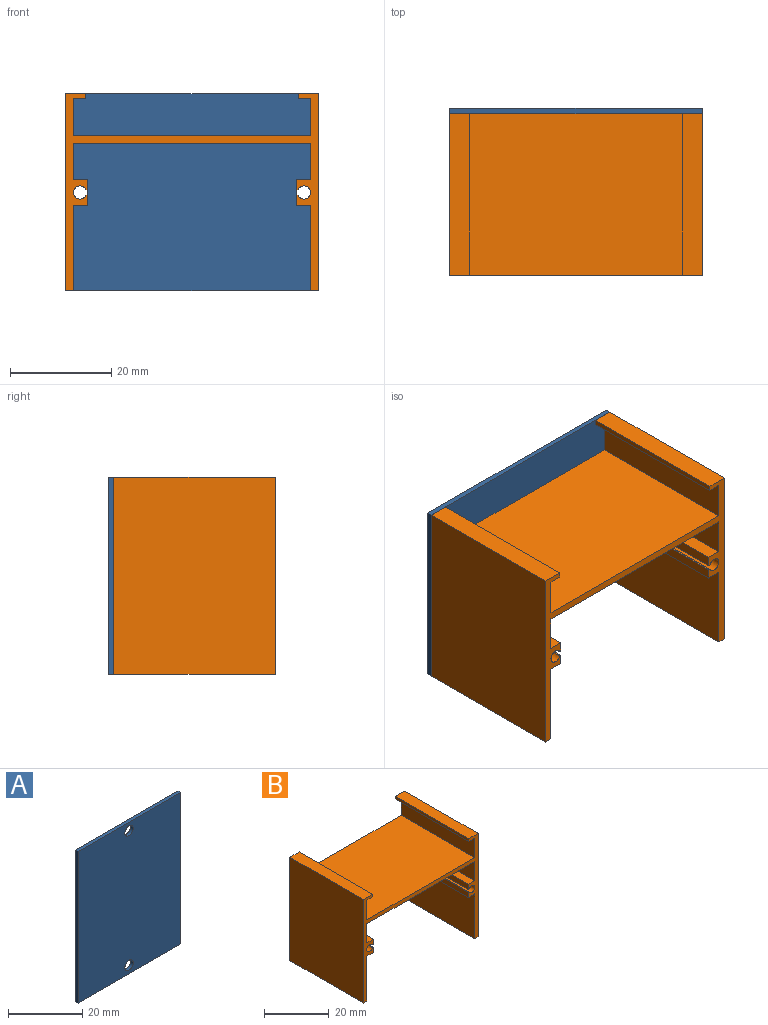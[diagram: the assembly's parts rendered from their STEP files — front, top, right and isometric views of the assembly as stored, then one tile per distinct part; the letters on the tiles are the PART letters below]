
ASSEMBLY  parts=2 mates=1
PART A: 8 faces, bbox 39x1x50 mm
  f0: plane 39x1mm, normal (0,0,-1), area 39mm2, adj f1,f3,f4,f5
  f1: plane 50x1mm, normal (1,0,0), area 50mm2, adj f0,f2,f4,f5
  f2: plane 39x1mm, normal (0,0,1), area 39mm2, adj f1,f3,f4,f5
  f3: plane 50x1mm, normal (-1,0,0), area 50mm2, adj f0,f2,f4,f5
  f4: plane 50x39mm, normal (0,-1,0), area 1933.9mm2, adj f0,f1,f2,f3,f6,f7
  f5: plane 50x39mm, normal (0,1,0), area 1933.9mm2, adj f0,f1,f2,f3,f6,f7
  f6: cylinder r=1.6mm len=3.2mm, axis (0,-1,0), area 10.1mm2, adj f4,f5
  f7: cylinder r=1.6mm len=3.2mm, axis (0,-1,0), area 10.1mm2, adj f4,f5
PART B: 34 faces, bbox 50x32x39 mm
  f0: plane 32x1.5mm, normal (0,0,-1), area 48mm2, adj f1,f31,f32,f33
  f1: plane 32x16.9mm, normal (1,0,0), area 540.8mm2, adj f0,f2,f32,f33
  f2: plane 32x2.8mm, normal (0,0,-1), area 89.6mm2, adj f1,f3,f32,f33
  f3: plane 32x2mm, normal (1,0,0), area 64mm2, adj f2,f4,f32,f33
  f4: plane 32x0.3mm, normal (0,0,1), area 9.6mm2, adj f3,f5,f32,f33
  f5: cylinder r=1.3mm len=32mm, axis (0,1,0), area 228.5mm2, adj f4,f6,f32,f33
  f6: plane 32x0.3mm, normal (0,0,-1), area 9.6mm2, adj f5,f7,f32,f33
  f7: plane 32x2mm, normal (1,0,0), area 64mm2, adj f6,f8,f32,f33
  f8: plane 32x2.8mm, normal (0,0,1), area 89.6mm2, adj f7,f9,f32,f33
  f9: plane 32x7.2mm, normal (1,0,0), area 230.4mm2, adj f8,f10,f32,f33
  f10: plane 47x32mm, normal (0,0,-1), area 1504mm2, adj f9,f11,f32,f33
  f11: plane 32x7.2mm, normal (-1,0,0), area 230.4mm2, adj f10,f12,f32,f33
  f12: plane 32x2.8mm, normal (0,0,1), area 89.6mm2, adj f11,f13,f32,f33
  f13: plane 32x2mm, normal (-1,0,0), area 64mm2, adj f12,f14,f32,f33
  f14: plane 32x0.3mm, normal (0,0,-1), area 9.6mm2, adj f13,f15,f32,f33
  f15: cylinder r=1.3mm len=32mm, axis (0,1,0), area 228.5mm2, adj f14,f16,f32,f33
  f16: plane 32x0.3mm, normal (0,0,1), area 9.6mm2, adj f15,f17,f32,f33
  f17: plane 32x2mm, normal (-1,0,0), area 64mm2, adj f16,f18,f32,f33
  f18: plane 32x2.8mm, normal (0,0,-1), area 89.6mm2, adj f17,f19,f32,f33
  f19: plane 32x16.9mm, normal (-1,0,0), area 540.8mm2, adj f18,f20,f32,f33
  f20: plane 32x1.5mm, normal (0,0,-1), area 48mm2, adj f19,f21,f32,f33
  f21: plane 39x32mm, normal (1,0,0), area 1248mm2, adj f20,f22,f32,f33
  f22: plane 32x4mm, normal (0,0,1), area 128mm2, adj f21,f23,f32,f33
  f23: plane 32x1mm, normal (-1,0,0), area 32mm2, adj f22,f24,f32,f33
  f24: plane 32x2.5mm, normal (0,0,-1), area 80mm2, adj f23,f25,f32,f33
  f25: plane 32x7.4mm, normal (-1,0,0), area 236.8mm2, adj f24,f26,f32,f33
  f26: plane 47x32mm, normal (0,0,1), area 1504mm2, adj f25,f27,f32,f33
  f27: plane 32x7.4mm, normal (1,0,0), area 236.8mm2, adj f26,f28,f32,f33
  f28: plane 32x2.5mm, normal (0,0,-1), area 80mm2, adj f27,f29,f32,f33
  f29: plane 32x1mm, normal (1,0,0), area 32mm2, adj f28,f30,f32,f33
  f30: plane 32x4mm, normal (0,0,1), area 128mm2, adj f29,f31,f32,f33
  f31: plane 39x32mm, normal (-1,0,0), area 1248mm2, adj f0,f30,f32,f33
  f32: plane 50x39mm, normal (0,-1,0), area 209.4mm2, adj f0,f1,f2,f3,f4,f5,f6,f7
  f33: plane 50x39mm, normal (0,1,0), area 209.4mm2, adj f0,f1,f2,f3,f4,f5,f6,f7
PLACE A rot(axis=(-0.71,0,-0.71),180deg) t=(-127.53,24.35,-7.84)mm
PLACE B t=(-127.53,24.35,-7.84)mm
MATE fastened B.f33 <-> A.f5  axis (0,1,0) through (-127.53,24.35,-3.91)mm
